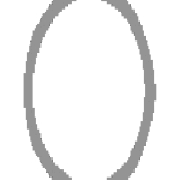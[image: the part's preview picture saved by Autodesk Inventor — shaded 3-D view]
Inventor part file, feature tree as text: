
AUTODESK INVENTOR PART (.ipt)
format: ipt  version: 2021 (Build 250183000, 183)  size: 110,080 bytes
history: native  units: in
note: dims shown in document units (in); Inventor stores cm internally (conversion verified against a paired STEP export)
features: other x4, sketch x3, plane x1
ambient origin geometry x8: Origin, YZ Plane, XZ Plane, XY Plane, X Axis, Y Axis, Z Axis, Center Point
bodies: Solid1 (feature_tree), Body (feature_tree)
feature tree (8):
  other  "Driven Length"
  other  "Frame Generator"
  other  "Start Plane"
  other  "End Plane"
  sketch  "Sketch"  dims[d2=11.6851in d4=-0.0in d5=11.6851in d6=0.12in d7=0.0in d8=90.0deg d9=11.6851in]
  sketch  "Sketch2"  dims[d0=1.0in]
  plane  "Work Plane3"
  sketch  "Sketch3"  dims[d1=0.065in]
